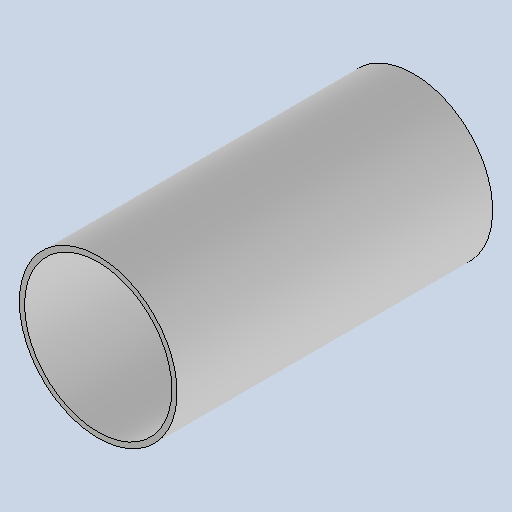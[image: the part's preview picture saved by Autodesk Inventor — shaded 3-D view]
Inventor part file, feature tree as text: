
AUTODESK INVENTOR PART (.ipt)
format: ipt  version: 2025.1 (Build 291241020, 241B)  size: 102,400 bytes
history: native  units: mm
features: extrude x1, sketch x1
ambient origin geometry x8: Origin, YZ Plane, XZ Plane, XY Plane, X Axis, Y Axis, Z Axis, Center Point
bodies: Solid1 (feature_tree)
feature tree (2):
  extrude  "Extrusion1"  Depth=180.0mm
  sketch  "Sketch1"  dims[d0=90.0mm d1=3.0mm d2=180.0mm d3=0.0mm]
